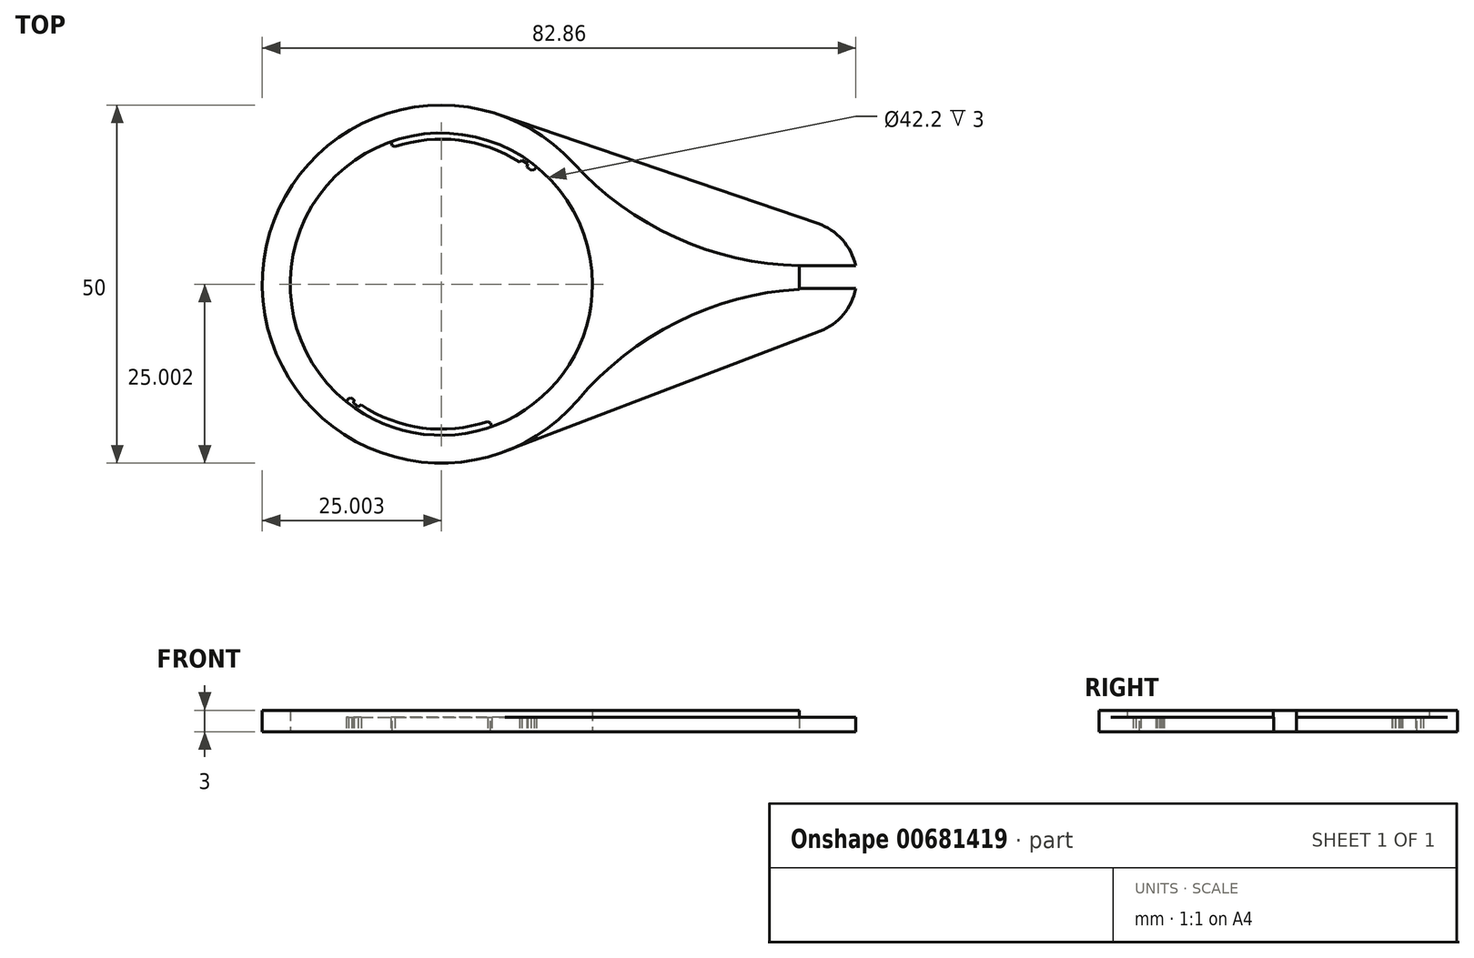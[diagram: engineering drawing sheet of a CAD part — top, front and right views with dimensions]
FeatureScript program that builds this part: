
annotation { "Feature Type Name" : "Feature", "Feature Type Description" : "" }
export const myFeature = defineFeature(function(context is Context, id is Id, definition is map)
    precondition{}
    {
        {
            var Q0;
            Q0=qCreatedBy(makeId("Top.planeOp"),FACE);
            var sketch = newSketch(context, id + "F0", { "sketchPlane" : qUnion([Q0])});
            skArc(sketch, "E0", {"start": v(-3.36, 18.49) * mm, "mid": v(-17.12, 2.18) * mm, "end": v(-9.62, -17.8) * mm});
            skArc(sketch, "E1", {"start": v(11.75, 22.25) * mm, "mid": v(-21.32, -1.85) * mm, "end": v(12.6, -24.76) * mm});
            skArc(sketch, "E2", {"start": v(-9.08, -17.14) * mm, "mid": v(0.23, -21.36) * mm, "end": v(10.42, -20.5) * mm});
            skLineSegment(sketch, "E3", {"start": v(16.43, 14.32) * mm, "end": v(16.96, 14.98) * mm});
            skLineSegment(sketch, "E4.MirrorCS", {"start": v(-3.07, 17.68) * mm, "end": v(-3.36, 18.49) * mm});
            skLineSegment(sketch, "E5.MirrorCS", {"start": v(-9.08, -17.14) * mm, "end": v(-9.62, -17.8) * mm});
            skLineSegment(sketch, "E6.MirrorCS", {"start": v(10.42, -20.5) * mm, "end": v(10.7, -21.3) * mm});
            skArc(sketch, "E7.trimOffspring", {"start": v(10.7, -21.3) * mm, "mid": v(24.47, -5) * mm, "end": v(16.96, 14.98) * mm});
            skArc(sketch, "E8.trimOffspring", {"start": v(16.43, 14.32) * mm, "mid": v(7.12, 18.55) * mm, "end": v(-3.07, 17.68) * mm});
            skLineSegment(sketch, "E9", {"start": v(3.67, -1.4) * mm, "end": v(3.23, 23.59) * mm, "construction": true});
            skLineSegment(sketch, "E10.0", {"start": v(2.18, 17.53) * mm, "end": v(16.96, 14.98) * mm, "construction": true});
            skLineSegment(sketch, "E10.1", {"start": v(2.18, 17.53) * mm, "end": v(3.23, 23.59) * mm, "construction": true});
            skLineSegment(sketch, "E11", {"start": v(3.67, -1.4) * mm, "end": v(70.37, -0.22) * mm, "construction": true});
            skArc(sketch, "E12", {"start": v(56.53, -7.99) * mm, "mid": v(59.8, -5.65) * mm, "end": v(61.53, -2.01) * mm});
            skLineSegment(sketch, "E13", {"start": v(11.75, 22.25) * mm, "end": v(56.26, 7.06) * mm});
            skLineSegment(sketch, "E14", {"start": v(12.6, -24.76) * mm, "end": v(56.53, -7.99) * mm});
            skLineSegment(sketch, "E15.bottom", {"start": v(61.5, 1.15) * mm, "end": v(53.67, 1.15) * mm});
            skLineSegment(sketch, "E15.top", {"start": v(61.53, -2.01) * mm, "end": v(53.67, -2.01) * mm});
            skLineSegment(sketch, "E15.right", {"start": v(53.67, 1.15) * mm, "end": v(53.67, -2.01) * mm});
            skPoint(sketch, "E16.orphan", {"position": v(63.02, 1.15) * mm});
            skArc(sketch, "E17.trimOffspring", {"start": v(61.5, 1.15) * mm, "mid": v(59.66, 4.8) * mm, "end": v(56.26, 7.06) * mm});
            skSolve(sketch);
        }
        {
            var Q0;
            Q0=makeQuery(id+"F0.imprint","IMPRINT",FACE,{"disambiguationData":[TD([[makeQuery(id+"F0.imprint","IMPRINT",EDGE,{"derivedFrom":sQuery(id+"F0.wireOp",EDGE,"E0")}),-1.0]])]});
            extrude(context, id + "F1", {"entities" : qUnion([Q0]), "depth" : 2 * mm, "offsetDistance" : 25 * mm});
        }
        {
            var Q0;
            Q0=makeQuery(id+"F1.opExtrude","CAP_FACE",FACE,{"disambiguationData":[OSD([sQuery(id+"F0.wireOp",EDGE,"E0"),sQuery(id+"F0.wireOp",EDGE,"E1"),sQuery(id+"F0.wireOp",EDGE,"E2"),sQuery(id+"F0.wireOp",EDGE,"E3"),sQuery(id+"F0.wireOp",EDGE,"E4.MirrorCS"),sQuery(id+"F0.wireOp",EDGE,"E5.MirrorCS"),sQuery(id+"F0.wireOp",EDGE,"E6.MirrorCS"),sQuery(id+"F0.wireOp",EDGE,"E7.trimOffspring"),sQuery(id+"F0.wireOp",EDGE,"E8.trimOffspring"),sQuery(id+"F0.wireOp",EDGE,"E12"),sQuery(id+"F0.wireOp",EDGE,"E13"),sQuery(id+"F0.wireOp",EDGE,"E14"),sQuery(id+"F0.wireOp",EDGE,"E15.bottom"),sQuery(id+"F0.wireOp",EDGE,"E15.top"),sQuery(id+"F0.wireOp",EDGE,"E15.right"),sQuery(id+"F0.wireOp",EDGE,"E17.trimOffspring")])],"isStart":false});
            var sketch = newSketch(context, id + "F2", { "sketchPlane" : qUnion([Q0])});
            skCircle(sketch, "E18", {"center": v(3.67, -1.4) * mm, "radius": 21.1 * mm});
            skArc(sketch, "E19", {"start": v(22.1, 15.5) * mm, "mid": v(-21.32, -1.88) * mm, "end": v(22.72, -17.6) * mm});
            skArc(sketch, "E20", {"start": v(22.1, 15.5) * mm, "mid": v(36.42, 5.1) * mm, "end": v(53.67, 1.17) * mm});
            skLineSegment(sketch, "E21", {"start": v(3.67, -1.4) * mm, "end": v(14.94, -1.4) * mm, "construction": true});
            skArc(sketch, "E22", {"start": v(53.67, -2.1) * mm, "mid": v(36.62, -6.7) * mm, "end": v(22.72, -17.6) * mm});
            skLineSegment(sketch, "E23", {"start": v(53.67, 1.17) * mm, "end": v(53.67, -2.1) * mm});
            skSolve(sketch);
        }
        {
            var Q0;
            {var subQ2=sQuery(id+"F2.wireOp",EDGE,"E20");Q0=makeQuery(id+"F2.imprint","IMPRINT",FACE,{"disambiguationData":[TD([[makeQuery(id+"F2.imprint","IMPRINT",EDGE,{"derivedFrom":subQ2}),-1.0]])]});}
            extrude(context, id + "F3", {"entities" : qUnion([Q0]), "operationType" : NewBodyOperationType.ADD, "depth" : 1 * mm, "offsetDistance" : 25 * mm});
        }
        {
            var Q0;
            Q0=makeQuery(id+"F1.opExtrude","CAP_FACE",FACE,{"disambiguationData":[OSD([sQuery(id+"F0.wireOp",EDGE,"E0"),sQuery(id+"F0.wireOp",EDGE,"E1"),sQuery(id+"F0.wireOp",EDGE,"E2"),sQuery(id+"F0.wireOp",EDGE,"E3"),sQuery(id+"F0.wireOp",EDGE,"E4.MirrorCS"),sQuery(id+"F0.wireOp",EDGE,"E5.MirrorCS"),sQuery(id+"F0.wireOp",EDGE,"E6.MirrorCS"),sQuery(id+"F0.wireOp",EDGE,"E7.trimOffspring"),sQuery(id+"F0.wireOp",EDGE,"E8.trimOffspring"),sQuery(id+"F0.wireOp",EDGE,"E12"),sQuery(id+"F0.wireOp",EDGE,"E13"),sQuery(id+"F0.wireOp",EDGE,"E14"),sQuery(id+"F0.wireOp",EDGE,"E15.bottom"),sQuery(id+"F0.wireOp",EDGE,"E15.top"),sQuery(id+"F0.wireOp",EDGE,"E15.right"),sQuery(id+"F0.wireOp",EDGE,"E17.trimOffspring")])],"isStart":true});
            var sketch = newSketch(context, id + "F4", { "sketchPlane" : qUnion([Q0])});
            skLineSegment(sketch, "E24", {"start": v(-8.47, 17.22) * mm, "end": v(-8.58, 17.98) * mm});
            skLineSegment(sketch, "E25", {"start": v(-8.58, 17.98) * mm, "end": v(-7.95, 18.49) * mm});
            skLineSegment(sketch, "E26", {"start": v(-7.95, 18.49) * mm, "end": v(-7.16, 18.1) * mm});
            skLineSegment(sketch, "E27", {"start": v(-7.16, 18.1) * mm, "end": v(-8.47, 17.22) * mm});
            skLineSegment(sketch, "E28", {"start": v(15.54, -14.45) * mm, "end": v(15.76, -15.4) * mm});
            skLineSegment(sketch, "E29", {"start": v(15.76, -15.4) * mm, "end": v(14.92, -15.92) * mm});
            skLineSegment(sketch, "E30", {"start": v(14.92, -15.92) * mm, "end": v(14.03, -15.25) * mm});
            skLineSegment(sketch, "E31", {"start": v(14.03, -15.25) * mm, "end": v(15.54, -14.45) * mm});
            skSolve(sketch);
        }
        {
            var Q0;
            Q0 = qSketchRegion(id + "F4", true);
            extrude(context, id + "F5", {"entities" : qUnion([Q0]), "operationType" : NewBodyOperationType.REMOVE, "oppositeDirection" : true, "depth" : 25 * mm, "offsetDistance" : 25 * mm});
        }
        {
            var Q0;
            Q0=makeQuery(id+"F1.opExtrude","SWEPT_EDGE",EDGE,{"disambiguationData":[OSD([sQuery(id+"F0.wireOp",EDGE,"E2"),sQuery(id+"F0.wireOp",EDGE,"E5.MirrorCS")])]});
            var Q1;
            Q1=makeQuery(id+"F1.opExtrude","SWEPT_EDGE",EDGE,{"disambiguationData":[OSD([sQuery(id+"F0.wireOp",EDGE,"E2"),sQuery(id+"F0.wireOp",EDGE,"E6.MirrorCS")])]});
            var Q2;
            Q2=makeQuery(id+"F1.opExtrude","SWEPT_EDGE",EDGE,{"disambiguationData":[OSD([sQuery(id+"F0.wireOp",EDGE,"E3"),sQuery(id+"F0.wireOp",EDGE,"E8.trimOffspring")])]});
            var Q3;
            Q3=makeQuery(id+"F1.opExtrude","SWEPT_EDGE",EDGE,{"disambiguationData":[OSD([sQuery(id+"F0.wireOp",EDGE,"E4.MirrorCS"),sQuery(id+"F0.wireOp",EDGE,"E8.trimOffspring")])]});
            chamfer(context, id + "F6", {"entities" : qUnion([Q0, Q1, Q2, Q3]), "width" : 0.3 * mm, "tangentPropagation" : true});
        }
    });
